# Revit family: Faucet-Kitchen-KOHLER-Coralais-K-15173_1
name_source: partatom
category: Plumbing Fixtures
units: mm (PartAtom-declared; Revit-internal decimal feet)

## family parameters
Cut with Voids When Loaded = No
Host = Face
OmniClass Number = 23.31.11.00
OmniClass Title = Faucets
Part Type = Normal
Room Calculation Point = No
Round Connector Dimension = Use Diameter
Shared = No

## types (3) — shared parameters
ADA Compliant = Yes
Assembly Code = D2010
CW Connection = Yes
Cold Water Inlet = Cold Water Inlet
Date Modified = 04/13/2023
Default Elevation = 36"
Description = Single-handle kitchen sink faucet with sidespray through escutcheon and 8-1/2Inches swing spout, project pack
Distance To Side Spray = 4 1/16"
Drain Included = No
Flow Rate = 2 GPM
HW Connection = Yes
Handle Clearance = 4 7/8"
Height = 7 9/16"
Hot Water Inlet = Hot Water Inlet
Length = 8 1/2"
Manufacturer = Kohler Co.
Master Format 2014 = 22 41 39
Master Format 2014 Name = Residential Faucets, Supplies, and Trim
Material = Premium Metal Construction
Pressure = 60.00 psi
Product Documentation Link = https://www.us.kohler.com
Product Name = Coralais
Product Page URL = http://www.us.kohler.com
Spout Reach = 8 1/2"
URL = http://www.us.kohler.com
Vent Connection = No
Waste Connection = No
Waste Water Outlet = Waste Water Outlet
WaterSense Certified = No
Width = 10 1/2"

## per-type parameters (varying)
| type | Finish | Model | Type |
| BN-Vibrant Brushed Nickel | Kohler-Metal-BN-Vibrant_Brushed_Nickel | K-P15173-F-BN | 1 |
| CP-Polished Chrome | Kohler-Metal-CP-Polished_Chrome | K-P15173-F-CP | 2 |
| G-Brushed Chrome | Kohler-Metal-G-Brushed_Chrome | K-P15173-F-G | 3 |

## geometry (parser evidence)
native form markers: Sweep x6
no freeform markers — native parametric forms only
